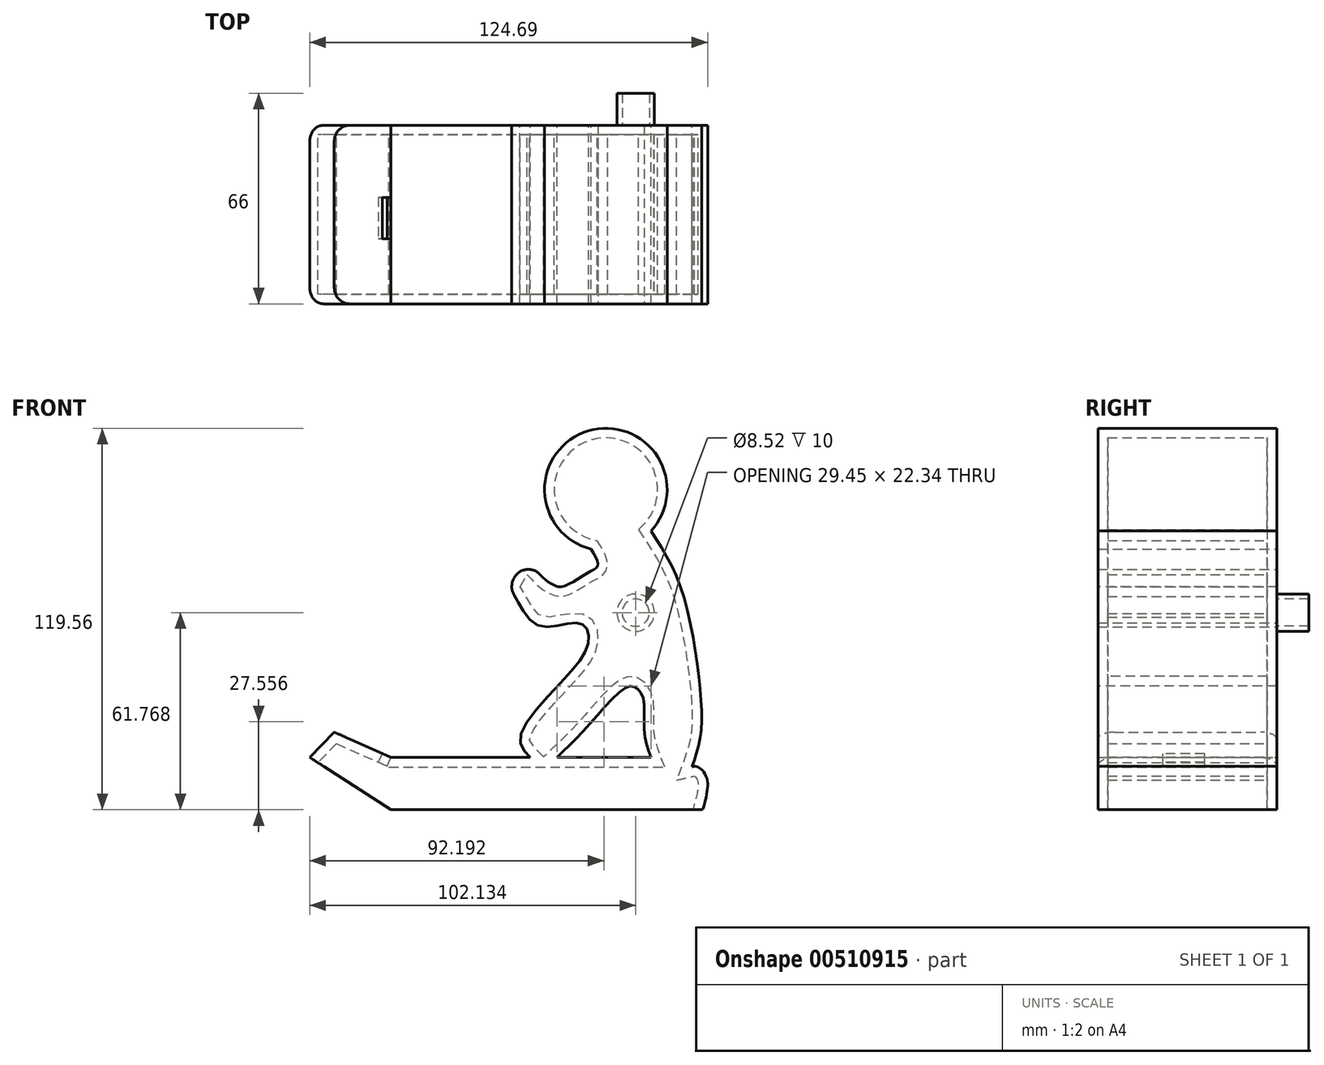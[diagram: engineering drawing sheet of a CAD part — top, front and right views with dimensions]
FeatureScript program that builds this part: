
annotation { "Feature Type Name" : "Feature", "Feature Type Description" : "" }
export const myFeature = defineFeature(function(context is Context, id is Id, definition is map)
    precondition{}
    {
        {
            var Q0;
            Q0=qCreatedBy(makeId("Front.planeOp"),FACE);
            var sketch = newSketch(context, id + "F0", { "sketchPlane" : qUnion([Q0])});
            skArc(sketch, "E0", {"start": v(30.65, 18.36) * mm, "mid": v(11.01, 49.77) * mm, "end": v(11.89, 12.74) * mm});
            skFitSpline(sketch, "E1", {"points": [v(30.65, 18.36) * mm, v(39.61, 1.72) * mm, v(45.73, -27.7) * mm, v(46.18, -46.04) * mm, v(43.46, -55.55) * mm], "startDerivative": vector(38.69, -58.74) * mm, "endDerivative": vector(-18.02, -48.66) * mm});
            skFitSpline(sketch, "E2", {"points": [v(43.46, -55.55) * mm, v(45.25, -55.55) * mm, v(48.2, -59.28) * mm, v(46.86, -68.98) * mm], "startDerivative": vector(8.36, 1.92) * mm, "endDerivative": vector(-6.56, -22.41) * mm});
            skFitSpline(sketch, "E3", {"points": [v(46.86, -68.98) * mm, v(-16.14, -68.98) * mm], "startDerivative": vector(-63, 0) * mm, "endDerivative": vector(-63, 0) * mm});
            skFitSpline(sketch, "E4", {"points": [v(-16.14, -68.98) * mm, v(-50.8, -68.98) * mm], "startDerivative": vector(-34.66, 0) * mm, "endDerivative": vector(-34.66, 0) * mm});
            skFitSpline(sketch, "E5", {"points": [v(-50.8, -68.98) * mm, v(-76.25, -52.6) * mm], "startDerivative": vector(-25.45, 16.39) * mm, "endDerivative": vector(-25.45, 16.39) * mm});
            skFitSpline(sketch, "E6", {"points": [v(-50.8, -52.6) * mm, v(30.67, -52.6) * mm], "startDerivative": vector(81.47, 0) * mm, "endDerivative": vector(81.47, 0) * mm});
            skFitSpline(sketch, "E7", {"points": [v(30.67, -52.6) * mm, v(28.59, -44.43) * mm, v(28.27, -34.19) * mm, v(25.86, -30.67) * mm, v(22.82, -30.67) * mm, v(11.46, -42.2) * mm, v(1.22, -52.6) * mm], "startDerivative": vector(-16.99, 46.45) * mm, "endDerivative": vector(-45.18, -43.3) * mm});
            skFitSpline(sketch, "E8", {"points": [v(-7.1, -52.6) * mm, v(-10.3, -46.03) * mm, v(5.38, -25.86) * mm, v(11.14, -16.1) * mm, v(9.86, -11.3) * mm, v(4.74, -10.66) * mm, v(-5.19, -10.98) * mm, v(-11.43, -2.98) * mm, v(-13.83, 0.7) * mm], "startDerivative": vector(-49.74, 49.64) * mm, "endDerivative": vector(-25.24, 34.65) * mm});
            skFitSpline(sketch, "E9", {"points": [v(-13.83, 0.7) * mm, v(-9.99, 7.59) * mm], "startDerivative": vector(3.84, 6.88) * mm, "endDerivative": vector(3.84, 6.88) * mm});
            skFitSpline(sketch, "E10", {"points": [v(-9.99, 7.59) * mm, v(-7.27, 7.59) * mm, v(-3.1, 3.75) * mm, v(0.1, 1.5) * mm, v(3.14, 1.02) * mm, v(10.98, 5.35) * mm, v(14.02, 7.59) * mm, v(11.89, 12.74) * mm], "startDerivative": vector(24.4, 5.79) * mm, "endDerivative": vector(-23.1, 37.98) * mm});
            skLineSegment(sketch, "E11", {"start": v(-68.57, -44.7) * mm, "end": v(-50.8, -52.6) * mm});
            skLineSegment(sketch, "E12", {"start": v(-68.57, -44.7) * mm, "end": v(-76.25, -52.6) * mm});
            skLineSegment(sketch, "E13", {"start": v(14.02, 50.42) * mm, "end": v(8.63, 48.88) * mm});
            skSolve(sketch);
        }
        {
            var Q0;
            Q0=makeQuery(id+"F0.imprint","IMPRINT",FACE,{"disambiguationData":[TD([[makeQuery(id+"F0.imprint","IMPRINT",EDGE,{"derivedFrom":sQuery(id+"F0.wireOp",EDGE,"E0")}),1.0]])]});
            var Q1;
            {var subQ4=sQuery(id+"F0.wireOp",EDGE,"E1");Q1=makeQuery(id+"F0.imprint","IMPRINT",FACE,{"disambiguationData":[TD([[makeQuery(id+"F0.imprint","IMPRINT",EDGE,{"derivedFrom":subQ4}),-1.0]])]});}
            extrude(context, id + "F1", {"entities" : qUnion([Q0, Q1]), "depth" : 56 * mm});
        }
        {
            var Q0;
            Q0=makeQuery(id+"F1.opExtrude","SWEPT_FACE",FACE,{"disambiguationData":[OSD([sQuery(id+"F0.wireOp",EDGE,"E3")])]});
            var Q1;
            Q1=makeQuery(id+"F1.opExtrude","SWEPT_FACE",FACE,{"disambiguationData":[OSD([sQuery(id+"F0.wireOp",EDGE,"E4")])]});
            var Q2;
            Q2=makeQuery(id+"F1.opExtrude","SWEPT_FACE",FACE,{"disambiguationData":[OSD([sQuery(id+"F0.wireOp",EDGE,"E5")])]});
            shell(context, id + "F2", {"entities" : qUnion([Q0, Q1, Q2]), "thickness" : 3 * mm});
        }
        {
            var Q0;
            Q0=makeQuery(id+"F1.opExtrude","CAP_EDGE",EDGE,{"disambiguationData":[OSD([sQuery(id+"F0.wireOp",EDGE,"E12")])],"isStart":false});
            var Q1;
            Q1=makeQuery(id+"F1.opExtrude","CAP_EDGE",EDGE,{"disambiguationData":[OSD([sQuery(id+"F0.wireOp",EDGE,"E12")])],"isStart":true});
            var Q2;
            Q2=makeQuery(id+"F1.opExtrude","SWEPT_EDGE",EDGE,{"disambiguationData":[OSD([sQuery(id+"F0.wireOp",EDGE,"E8"),sQuery(id+"F0.wireOp",EDGE,"E9")])]});
            var Q3;
            Q3=makeQuery(id+"F1.opExtrude","SWEPT_EDGE",EDGE,{"disambiguationData":[OSD([sQuery(id+"F0.wireOp",EDGE,"E9"),sQuery(id+"F0.wireOp",EDGE,"E10")])]});
            fillet(context, id + "F3", {"entities" : qUnion([Q0, Q1, Q2, Q3]), "radius" : 5 * mm, "tangentPropagation" : true, "allowEdgeOverflow" : false});
        }
        {
            var Q0;
            Q0=makeQuery(id+"F1.opExtrude","SWEPT_FACE",FACE,{"disambiguationData":[OSD([sQuery(id+"F0.wireOp",EDGE,"E11")])]});
            var sketch = newSketch(context, id + "F4", { "sketchPlane" : qUnion([Q0])});
            skLineSegment(sketch, "E14.bottom", {"start": v(-25.1, -22.6) * mm, "end": v(-28.1, -22.6) * mm});
            skLineSegment(sketch, "E14.top", {"start": v(-25.1, -35.6) * mm, "end": v(-28.1, -35.6) * mm});
            skLineSegment(sketch, "E14.left", {"start": v(-25.1, -22.6) * mm, "end": v(-25.1, -35.6) * mm});
            skLineSegment(sketch, "E14.right", {"start": v(-28.1, -22.6) * mm, "end": v(-28.1, -35.6) * mm});
            skLineSegment(sketch, "E15", {"start": v(-25.1, -13.16) * mm, "end": v(-25.1, -38.19) * mm, "construction": true});
            skLineSegment(sketch, "E16.MirrorCS", {"start": v(-25.1, -35.6) * mm, "end": v(-22.1, -35.6) * mm});
            skLineSegment(sketch, "E17.MirrorCS", {"start": v(-25.1, -22.6) * mm, "end": v(-22.1, -22.6) * mm});
            skLineSegment(sketch, "E18.MirrorCS", {"start": v(-22.1, -22.6) * mm, "end": v(-22.1, -35.6) * mm});
            skSolve(sketch);
        }
        {
            var Q0;
            Q0=makeQuery(id+"F4.imprint","IMPRINT",FACE,{"disambiguationData":[TD([[makeQuery(id+"F4.imprint","IMPRINT",EDGE,{"derivedFrom":sQuery(id+"F4.wireOp",EDGE,"E14.bottom")}),1.0]])]});
            extrude(context, id + "F5", {"entities" : qUnion([Q0]), "operationType" : NewBodyOperationType.REMOVE, "oppositeDirection" : true, "depth" : 25 * mm});
        }
        {
            var Q0;
            Q0=qCreatedBy(makeId("Front.planeOp"),FACE);
            var sketch = newSketch(context, id + "F6", { "sketchPlane" : qUnion([Q0])});
            skCircle(sketch, "E19", {"center": v(25.88, -7.21) * mm, "radius": 5.88 * mm});
            skCircle(sketch, "E20", {"center": v(25.88, -7.21) * mm, "radius": 4.26 * mm});
            skSolve(sketch);
        }
        {
            var Q0;
            Q0=makeQuery(id+"F6.imprint","IMPRINT",FACE,{"disambiguationData":[TD([[makeQuery(id+"F6.imprint","IMPRINT",EDGE,{"derivedFrom":sQuery(id+"F6.wireOp",EDGE,"E19")}),1.0]])]});
            extrude(context, id + "F7", {"entities" : qUnion([Q0]), "operationType" : NewBodyOperationType.ADD, "oppositeDirection" : true, "depth" : 10 * mm, "offsetDistance" : 25 * mm});
        }
    });
